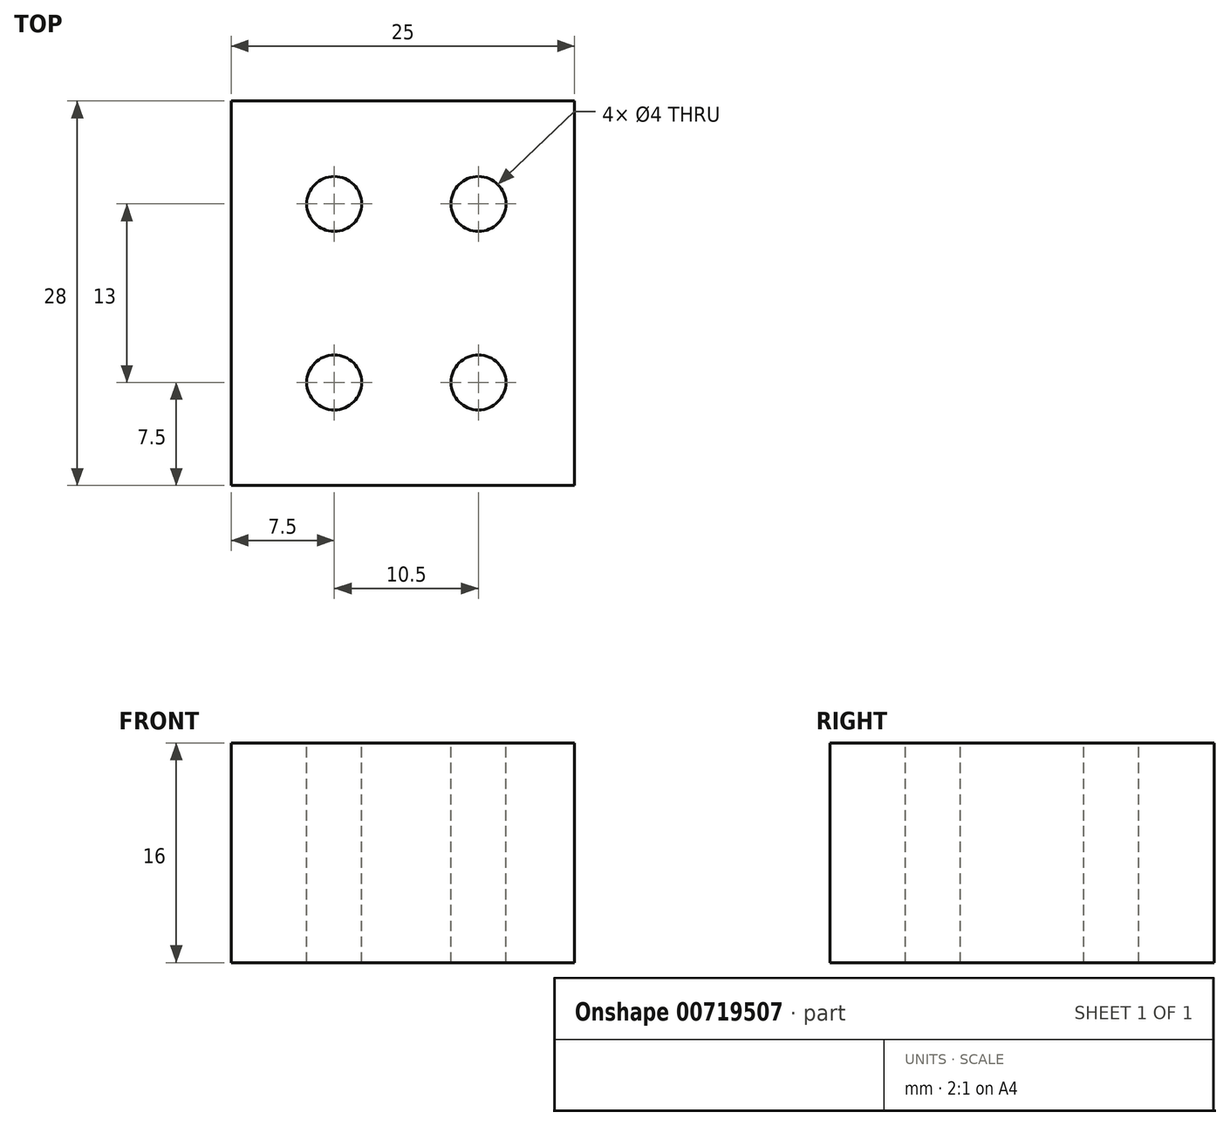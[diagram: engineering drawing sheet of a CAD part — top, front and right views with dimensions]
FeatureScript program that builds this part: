
annotation { "Feature Type Name" : "Feature", "Feature Type Description" : "" }
export const myFeature = defineFeature(function(context is Context, id is Id, definition is map)
    precondition{}
    {
        {
            var Q0;
            Q0=qCreatedBy(makeId("Top.planeOp"),FACE);
            var sketch = newSketch(context, id + "F0", { "sketchPlane" : qUnion([Q0])});
            skLineSegment(sketch, "E0.bottom", {"start": v(14, -14) * mm, "end": v(-14, -14) * mm});
            skLineSegment(sketch, "E0.top", {"start": v(14, 14) * mm, "end": v(-14, 14) * mm});
            skLineSegment(sketch, "E0.left", {"start": v(14, -14) * mm, "end": v(14, 14) * mm});
            skLineSegment(sketch, "E0.right", {"start": v(-14, -14) * mm, "end": v(-14, 14) * mm});
            skPoint(sketch, "E0.middle", {"position": v(0, 0) * mm});
            skSolve(sketch);
        }
        {
            var Q0;
            Q0=makeQuery(id+"F0.imprint","IMPRINT",FACE,{"disambiguationData":[TD([[makeQuery(id+"F0.imprint","IMPRINT",EDGE,{"derivedFrom":sQuery(id+"F0.wireOp",EDGE,"E0.bottom")}),-1.0]])]});
            extrude(context, id + "F1", {"entities" : qUnion([Q0]), "depth" : 16 * mm, "offsetDistance" : 25 * mm});
        }
        {
            var Q0;
            Q0=makeQuery(id+"F1.opExtrude","CAP_FACE",FACE,{"disambiguationData":[OSD([sQuery(id+"F0.wireOp",EDGE,"E0.bottom"),sQuery(id+"F0.wireOp",EDGE,"E0.top"),sQuery(id+"F0.wireOp",EDGE,"E0.left"),sQuery(id+"F0.wireOp",EDGE,"E0.right")])],"isStart":false});
            var sketch = newSketch(context, id + "F2", { "sketchPlane" : qUnion([Q0])});
            skPoint(sketch, "E1", {"position": v(4, -6.5) * mm});
            skPoint(sketch, "E2", {"position": v(-6.5, 6.5) * mm});
            skPoint(sketch, "E3", {"position": v(4, 6.5) * mm});
            skPoint(sketch, "E4", {"position": v(-6.5, -6.5) * mm});
            skSolve(sketch);
        }
        {
            var Q0;
            Q0=sQuery(id+"F2.wireOp",VERTEX,"E1");
            var Q1;
            Q1=sQuery(id+"F2.wireOp",VERTEX,"E4");
            var Q2;
            Q2=sQuery(id+"F2.wireOp",VERTEX,"E2");
            var Q3;
            Q3=sQuery(id+"F2.wireOp",VERTEX,"E3");
            var Q4;
            Q4=makeQuery(id+"F1.opExtrude","SWEPT_BODY",BODY,{"disambiguationData":[OSD([sQuery(id+"F0.wireOp",EDGE,"E0.bottom"),sQuery(id+"F0.wireOp",EDGE,"E0.top"),sQuery(id+"F0.wireOp",EDGE,"E0.left"),sQuery(id+"F0.wireOp",EDGE,"E0.right")])]});
            hole(context, id + "F3", {"style" : HoleStyle.SIMPLE, "endStyle" : HoleEndStyle.THROUGH, "holeDiameter" : 4 * mm, "majorDiameter" : 5 * mm, "isTappedThrough" : true, "tappedDepth" : 12 * mm, "tapClearance" : 3, "locations" : qUnion([Q0, Q1, Q2, Q3]), "scope" : qUnion([Q4])});
        }
        {
            var Q0;
            Q0=makeQuery(id+"F1.opExtrude","SWEPT_FACE",FACE,{"disambiguationData":[OSD([sQuery(id+"F0.wireOp",EDGE,"E0.left")])]});
            extrude(context, id + "F4", {"entities" : qUnion([Q0]), "operationType" : NewBodyOperationType.REMOVE, "oppositeDirection" : true, "depth" : 3 * mm, "offsetDistance" : 25 * mm});
        }
    });
